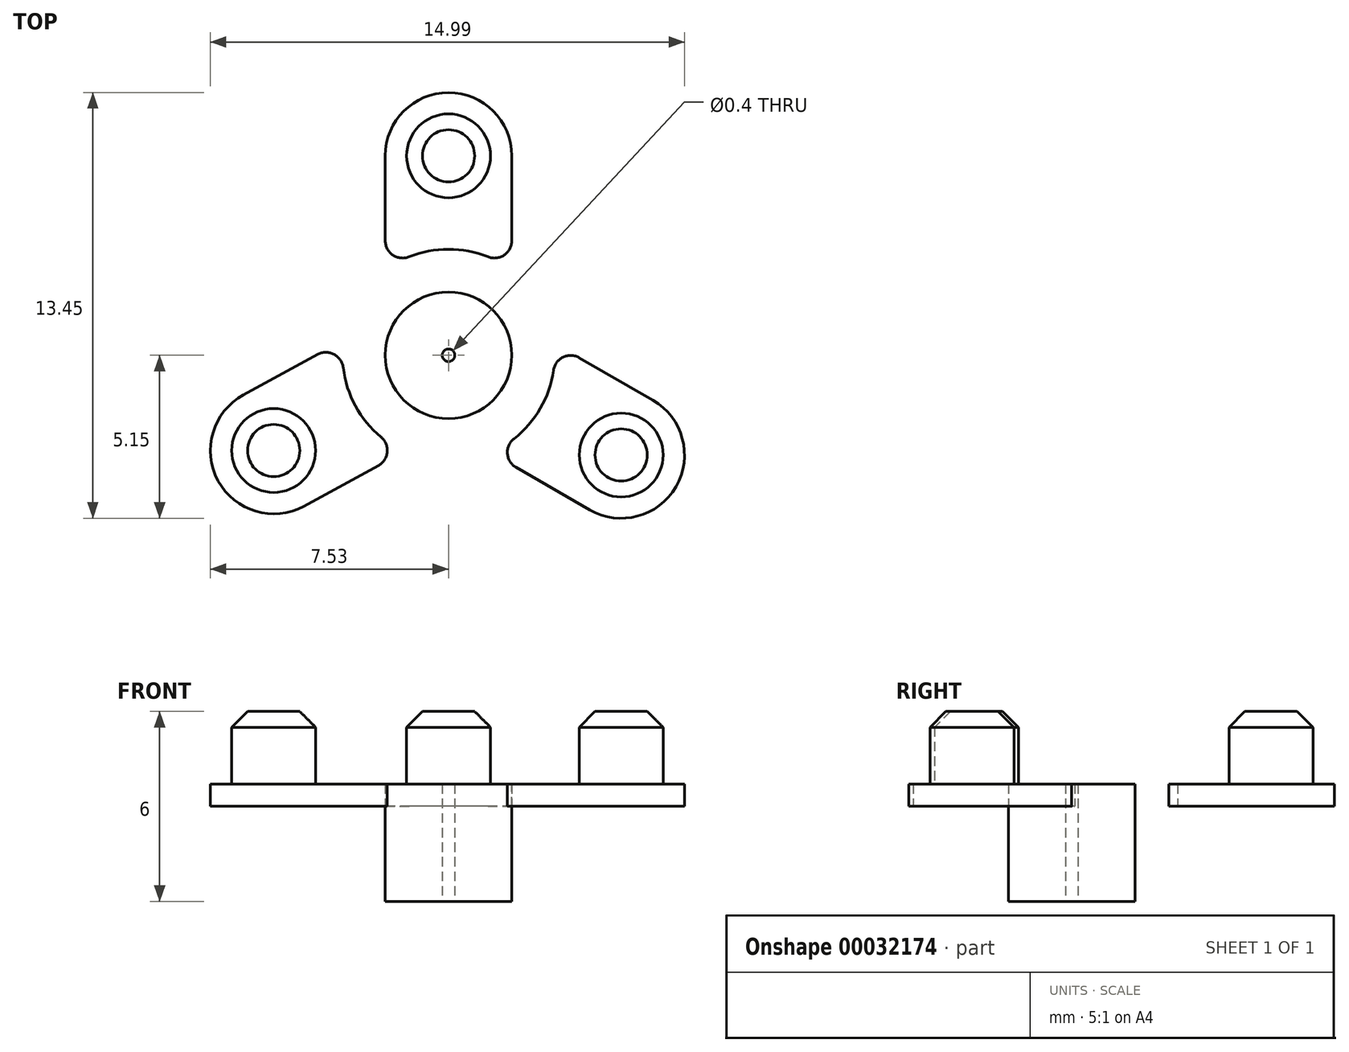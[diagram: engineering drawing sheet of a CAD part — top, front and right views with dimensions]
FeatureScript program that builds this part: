
annotation { "Feature Type Name" : "Feature", "Feature Type Description" : "" }
export const myFeature = defineFeature(function(context is Context, id is Id, definition is map)
    precondition{}
    {
        {
            var Q0;
            Q0=qCreatedBy(makeId("Top.planeOp"),FACE);
            var sketch = newSketch(context, id + "F0", { "sketchPlane" : qUnion([Q0])});
            skCircle(sketch, "E0", {"center": v(0, 0) * mm, "radius": 32.06 * mm});
            skCircle(sketch, "E1", {"center": v(0, 0) * mm, "radius": 0.2 * mm});
            skCircle(sketch, "E2", {"center": v(0, 0) * mm, "radius": 10.35 * mm});
            skCircle(sketch, "E3", {"center": v(0, 6.3) * mm, "radius": 0.2 * mm});
            skCircle(sketch, "E4", {"center": v(5.46, -3.15) * mm, "radius": 0.2 * mm});
            skCircle(sketch, "E5", {"center": v(-5.53, -3) * mm, "radius": 0.2 * mm});
            skLineSegment(sketch, "E6", {"start": v(-0.45, 10.34) * mm, "end": v(0.3, 10.35) * mm});
            skCircle(sketch, "E7", {"center": v(0, 6.3) * mm, "radius": 1.32 * mm});
            skCircle(sketch, "E8", {"center": v(0, 0) * mm, "radius": 3.35 * mm});
            skCircle(sketch, "E9", {"center": v(-5.53, -3) * mm, "radius": 1.32 * mm});
            skCircle(sketch, "E10", {"center": v(5.46, -3.15) * mm, "radius": 1.32 * mm});
            skLineSegment(sketch, "E11", {"start": v(-1.85, 2.81) * mm, "end": v(-1.85, 2.8) * mm});
            skArc(sketch, "E12.0.startCap", {"start": v(-0.96, 1.76) * mm, "mid": v(1.76, 0.96) * mm, "end": v(0.96, -1.76) * mm});
            skArc(sketch, "E12.0.endCap", {"start": v(-4.57, -4.77) * mm, "mid": v(-7.28, -3.97) * mm, "end": v(-6.48, -1.25) * mm});
            skArc(sketch, "E13.0.startCap", {"start": v(-1, -1.73) * mm, "mid": v(-1.73, 1) * mm, "end": v(1, 1.73) * mm});
            skArc(sketch, "E13.0.endCap", {"start": v(6.46, -1.42) * mm, "mid": v(7.19, -4.15) * mm, "end": v(4.46, -4.88) * mm});
            skArc(sketch, "E14.0.startCap", {"start": v(2, 0) * mm, "mid": v(0, -2) * mm, "end": v(-2, 0) * mm});
            skArc(sketch, "E14.0.endCap", {"start": v(-2, 6.3) * mm, "mid": v(0, 8.3) * mm, "end": v(2, 6.3) * mm});
            skLineSegment(sketch, "E15.trimOffspring", {"start": v(-2, 2.69) * mm, "end": v(-2, 6.3) * mm});
            skLineSegment(sketch, "E16.trimOffspring", {"start": v(-3.32, 0.47) * mm, "end": v(-6.48, -1.25) * mm});
            skLineSegment(sketch, "E17.trimOffspring", {"start": v(-1.4, -3.04) * mm, "end": v(-4.57, -4.77) * mm});
            skLineSegment(sketch, "E18.trimOffspring", {"start": v(1.33, -3.08) * mm, "end": v(4.46, -4.88) * mm});
            skLineSegment(sketch, "E19.trimOffspring", {"start": v(3.33, 0.39) * mm, "end": v(6.46, -1.42) * mm});
            skLineSegment(sketch, "E20.trimOffspring", {"start": v(2, 2.69) * mm, "end": v(2, 6.3) * mm});
            skSolve(sketch);
        }
        {
            var Q0;
            Q0=makeQuery(id+"F0.imprint","IMPRINT",FACE,{"disambiguationData":[TD([[makeQuery(id+"F0.imprint","IMPRINT",EDGE,{"derivedFrom":sQuery(id+"F0.wireOp",EDGE,"E7")}),-1.0]])]});
            var Q1;
            {var subQ5=sQuery(id+"F0.wireOp",EDGE,"E12.0.startCap");Q1=makeQuery(id+"F0.imprint","IMPRINT",FACE,{"disambiguationData":[TD([[makeQuery(id+"F0.imprint","IMPRINT",EDGE,{"derivedFrom":subQ5}),1.0]])]});}
            var Q2;
            Q2=makeQuery(id+"F0.imprint","IMPRINT",FACE,{"disambiguationData":[TD([[makeQuery(id+"F0.imprint","IMPRINT",EDGE,{"derivedFrom":sQuery(id+"F0.wireOp",EDGE,"E9")}),-1.0]])]});
            var Q3;
            Q3=makeQuery(id+"F0.imprint","IMPRINT",FACE,{"disambiguationData":[TD([[makeQuery(id+"F0.imprint","IMPRINT",EDGE,{"derivedFrom":sQuery(id+"F0.wireOp",EDGE,"E10")}),-1.0]])]});
            var Q4;
            Q4=makeQuery(id+"F0.imprint","IMPRINT",FACE,{"disambiguationData":[TD([[makeQuery(id+"F0.imprint","IMPRINT",EDGE,{"derivedFrom":sQuery(id+"F0.wireOp",EDGE,"E3")}),1.0]])]});
            var Q5;
            Q5=makeQuery(id+"F0.imprint","IMPRINT",FACE,{"disambiguationData":[TD([[makeQuery(id+"F0.imprint","IMPRINT",EDGE,{"derivedFrom":sQuery(id+"F0.wireOp",EDGE,"E5")}),1.0]])]});
            var Q6;
            Q6=makeQuery(id+"F0.imprint","IMPRINT",FACE,{"disambiguationData":[TD([[makeQuery(id+"F0.imprint","IMPRINT",EDGE,{"derivedFrom":sQuery(id+"F0.wireOp",EDGE,"E4")}),1.0]])]});
            extrude(context, id + "F1", {"entities" : qUnion([Q0, Q1, Q2, Q3, Q4, Q5, Q6]), "depth" : .7 * mm});
        }
        {
            var Q0;
            Q0=makeQuery(id+"F0.imprint","IMPRINT",FACE,{"disambiguationData":[TD([[makeQuery(id+"F0.imprint","IMPRINT",EDGE,{"derivedFrom":sQuery(id+"F0.wireOp",EDGE,"E3")}),1.0]])]});
            var Q1;
            Q1=makeQuery(id+"F0.imprint","IMPRINT",FACE,{"disambiguationData":[TD([[makeQuery(id+"F0.imprint","IMPRINT",EDGE,{"derivedFrom":sQuery(id+"F0.wireOp",EDGE,"E3")}),-1.0]])]});
            var Q2;
            Q2=makeQuery(id+"F0.imprint","IMPRINT",FACE,{"disambiguationData":[TD([[makeQuery(id+"F0.imprint","IMPRINT",EDGE,{"derivedFrom":sQuery(id+"F0.wireOp",EDGE,"E5")}),1.0]])]});
            var Q3;
            Q3=makeQuery(id+"F0.imprint","IMPRINT",FACE,{"disambiguationData":[TD([[makeQuery(id+"F0.imprint","IMPRINT",EDGE,{"derivedFrom":sQuery(id+"F0.wireOp",EDGE,"E5")}),-1.0]])]});
            var Q4;
            Q4=makeQuery(id+"F0.imprint","IMPRINT",FACE,{"disambiguationData":[TD([[makeQuery(id+"F0.imprint","IMPRINT",EDGE,{"derivedFrom":sQuery(id+"F0.wireOp",EDGE,"E4")}),1.0]])]});
            var Q5;
            Q5=makeQuery(id+"F0.imprint","IMPRINT",FACE,{"disambiguationData":[TD([[makeQuery(id+"F0.imprint","IMPRINT",EDGE,{"derivedFrom":sQuery(id+"F0.wireOp",EDGE,"E4")}),-1.0]])]});
            extrude(context, id + "F2", {"entities" : qUnion([Q0, Q1, Q2, Q3, Q4, Q5]), "operationType" : NewBodyOperationType.ADD, "depth" : 3 * mm});
        }
        {
            var Q0;
            {var subQ5=sQuery(id+"F0.wireOp",EDGE,"E12.0.startCap");Q0=makeQuery(id+"F0.imprint","IMPRINT",FACE,{"disambiguationData":[TD([[makeQuery(id+"F0.imprint","IMPRINT",EDGE,{"derivedFrom":subQ5}),1.0]])]});}
            extrude(context, id + "F3", {"entities" : qUnion([Q0]), "operationType" : NewBodyOperationType.ADD, "oppositeDirection" : true, "depth" : 3 * mm});
        }
        {
            var Q0;
            Q0=makeQuery(id+"F1.opExtrude","SWEPT_EDGE",EDGE,{"disambiguationData":[OSD([sQuery(id+"F0.wireOp",EDGE,"E8"),sQuery(id+"F0.wireOp",EDGE,"E15.trimOffspring")])]});
            var Q1;
            Q1=makeQuery(id+"F1.opExtrude","SWEPT_EDGE",EDGE,{"disambiguationData":[OSD([sQuery(id+"F0.wireOp",EDGE,"E8"),sQuery(id+"F0.wireOp",EDGE,"E16.trimOffspring")])]});
            var Q2;
            Q2=makeQuery(id+"F1.opExtrude","SWEPT_EDGE",EDGE,{"disambiguationData":[OSD([sQuery(id+"F0.wireOp",EDGE,"E8"),sQuery(id+"F0.wireOp",EDGE,"E17.trimOffspring")])]});
            var Q3;
            Q3=makeQuery(id+"F1.opExtrude","SWEPT_EDGE",EDGE,{"disambiguationData":[OSD([sQuery(id+"F0.wireOp",EDGE,"E8"),sQuery(id+"F0.wireOp",EDGE,"E18.trimOffspring")])]});
            var Q4;
            Q4=makeQuery(id+"F1.opExtrude","SWEPT_EDGE",EDGE,{"disambiguationData":[OSD([sQuery(id+"F0.wireOp",EDGE,"E8"),sQuery(id+"F0.wireOp",EDGE,"E19.trimOffspring")])]});
            var Q5;
            Q5=makeQuery(id+"F1.opExtrude","SWEPT_EDGE",EDGE,{"disambiguationData":[OSD([sQuery(id+"F0.wireOp",EDGE,"E8"),sQuery(id+"F0.wireOp",EDGE,"E20.trimOffspring")])]});
            var Q6;
            {var subQ0=sQuery(id+"F0.wireOp",EDGE,"E8");var subQ2=sQuery(id+"F0.wireOp",EDGE,"E15.trimOffspring");Q6=makeQuery(id+"F3.boolean.opBoolean","SPLIT",EDGE,{"disambiguationData":[TD([makeQuery(id+"F1.opExtrude","SWEPT_FACE",FACE,{"disambiguationData":[OSD([subQ2])]})])],"derivedFrom":makeQuery(id+"F3.opExtrude","CAP_EDGE",EDGE,{"disambiguationData":[OSD([subQ0])],"isStart":true})});}
            var Q7;
            {var subQ0=sQuery(id+"F0.wireOp",EDGE,"E8");var subQ2=sQuery(id+"F0.wireOp",EDGE,"E18.trimOffspring");Q7=makeQuery(id+"F3.boolean.opBoolean","SPLIT",EDGE,{"disambiguationData":[TD([makeQuery(id+"F1.opExtrude","SWEPT_FACE",FACE,{"disambiguationData":[OSD([subQ2])]})])],"derivedFrom":makeQuery(id+"F3.opExtrude","CAP_EDGE",EDGE,{"disambiguationData":[OSD([subQ0])],"isStart":true})});}
            var Q8;
            {var subQ0=sQuery(id+"F0.wireOp",EDGE,"E8");var subQ2=sQuery(id+"F0.wireOp",EDGE,"E16.trimOffspring");Q8=makeQuery(id+"F3.boolean.opBoolean","SPLIT",EDGE,{"disambiguationData":[TD([makeQuery(id+"F1.opExtrude","SWEPT_FACE",FACE,{"disambiguationData":[OSD([subQ2])]})])],"derivedFrom":makeQuery(id+"F3.opExtrude","CAP_EDGE",EDGE,{"disambiguationData":[OSD([subQ0])],"isStart":true})});}
            fillet(context, id + "F4", {"entities" : qUnion([Q0, Q1, Q2, Q3, Q4, Q5, Q6, Q7, Q8]), "radius" : .55 * mm, "tangentPropagation" : true, "allowEdgeOverflow" : false});
        }
        {
            var Q0;
            Q0=makeQuery(id+"F2.opExtrude","CAP_FACE",FACE,{"disambiguationData":[OSD([sQuery(id+"F0.wireOp",EDGE,"E9")])],"isStart":false});
            var Q1;
            Q1=makeQuery(id+"F2.opExtrude","CAP_FACE",FACE,{"disambiguationData":[OSD([sQuery(id+"F0.wireOp",EDGE,"E7")])],"isStart":false});
            var Q2;
            Q2=makeQuery(id+"F2.opExtrude","CAP_FACE",FACE,{"disambiguationData":[OSD([sQuery(id+"F0.wireOp",EDGE,"E10")])],"isStart":false});
            var Q3;
            Q3=makeQuery(id+"F3.opExtrude","CAP_EDGE",EDGE,{"disambiguationData":[OSD([sQuery(id+"F0.wireOp",EDGE,"E8")])],"isStart":false});
            chamfer(context, id + "F5", {"entities" : qUnion([Q0, Q1, Q2, Q3]), "width" : .5 * mm, "tangentPropagation" : true});
        }
    });
